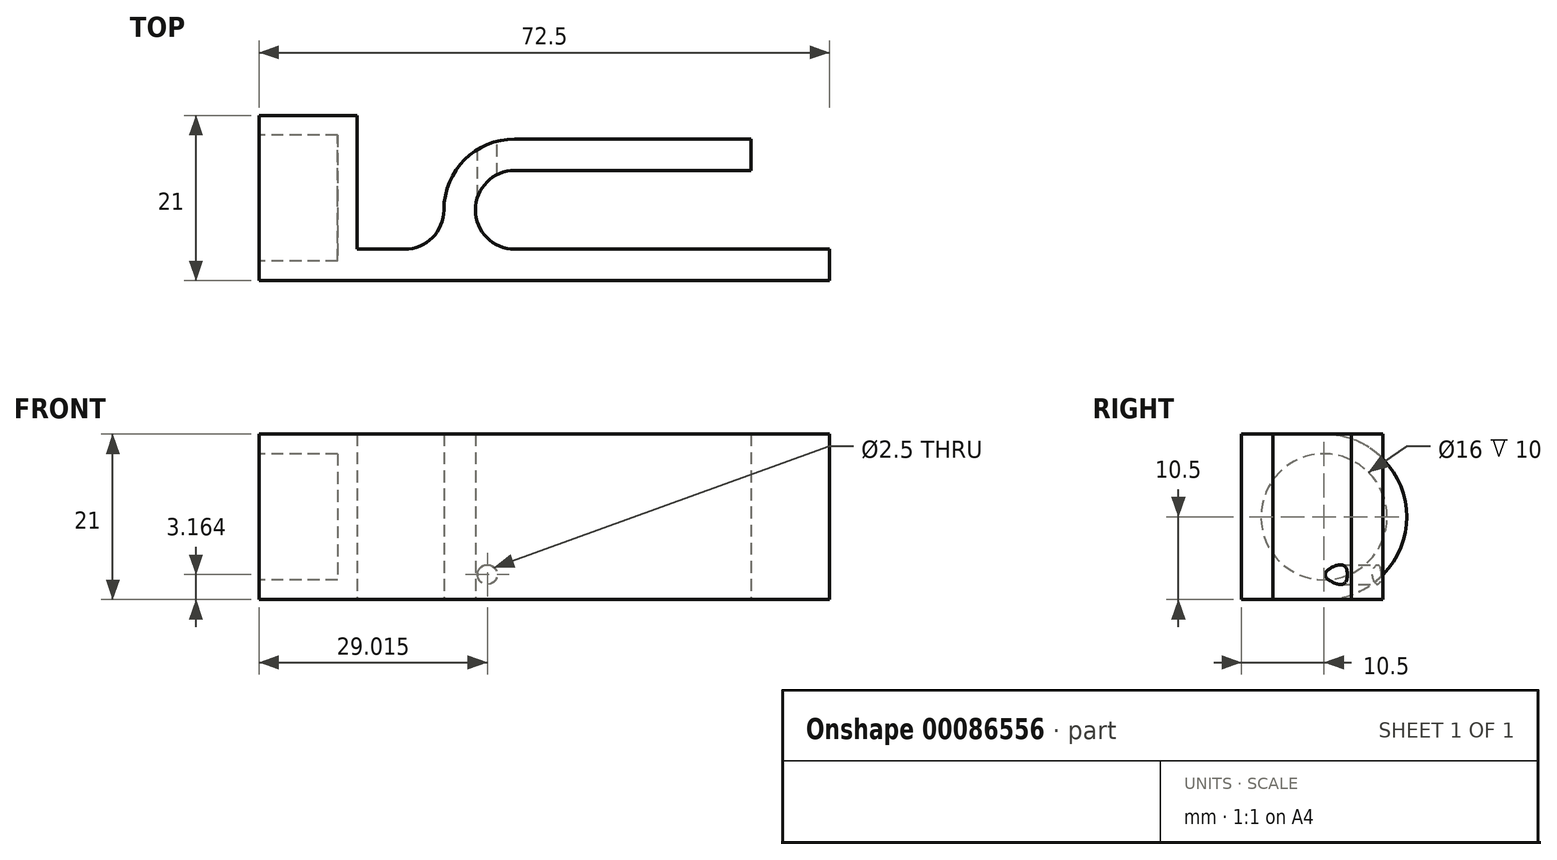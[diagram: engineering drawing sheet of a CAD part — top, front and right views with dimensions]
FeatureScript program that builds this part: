
annotation { "Feature Type Name" : "Feature", "Feature Type Description" : "" }
export const myFeature = defineFeature(function(context is Context, id is Id, definition is map)
    precondition{}
    {
        {
            var Q0;
            Q0=qCreatedBy(makeId("Top.planeOp"),FACE);
            var sketch = newSketch(context, id + "F0", { "sketchPlane" : qUnion([Q0])});
            skLineSegment(sketch, "E0", {"start": v(0, 0) * mm, "end": v(60, 0) * mm});
            skLineSegment(sketch, "E1", {"start": v(60, 0) * mm, "end": v(60, 4) * mm});
            skLineSegment(sketch, "E2", {"start": v(60, 4) * mm, "end": v(20, 4) * mm});
            skLineSegment(sketch, "E3", {"start": v(15, 9) * mm, "end": v(15, 9) * mm});
            skLineSegment(sketch, "E4", {"start": v(20, 14) * mm, "end": v(50, 14) * mm});
            skLineSegment(sketch, "E5", {"start": v(50, 14) * mm, "end": v(50, 18) * mm});
            skLineSegment(sketch, "E6", {"start": v(50, 18) * mm, "end": v(20, 18) * mm});
            skLineSegment(sketch, "E7", {"start": v(11, 9) * mm, "end": v(11, 9) * mm});
            skLineSegment(sketch, "E8", {"start": v(6, 4) * mm, "end": v(0, 4) * mm});
            skPoint(sketch, "E9.visualSharp", {"position": v(15, 14) * mm});
            skArc(sketch, "E9.filletArc", {"start": v(20, 14) * mm, "mid": v(16.46, 12.54) * mm, "end": v(15, 9) * mm});
            skPoint(sketch, "E10.visualSharp", {"position": v(11, 18) * mm});
            skArc(sketch, "E10.filletArc", {"start": v(20, 18) * mm, "mid": v(13.64, 15.36) * mm, "end": v(11, 9) * mm});
            skPoint(sketch, "E11.visualSharp", {"position": v(15, 4) * mm});
            skArc(sketch, "E11.filletArc", {"start": v(15, 9) * mm, "mid": v(16.46, 5.46) * mm, "end": v(20, 4) * mm});
            skPoint(sketch, "E12.visualSharp", {"position": v(11, 4) * mm});
            skArc(sketch, "E12.filletArc", {"start": v(6, 4) * mm, "mid": v(9.54, 5.46) * mm, "end": v(11, 9) * mm});
            skLineSegment(sketch, "E13", {"start": v(0, 4) * mm, "end": v(0, 0) * mm});
            skSolve(sketch);
        }
        {
            var Q0;
            Q0=makeQuery(id+"F0.imprint","IMPRINT",FACE,{"disambiguationData":[TD([[makeQuery(id+"F0.imprint","IMPRINT",EDGE,{"derivedFrom":sQuery(id+"F0.wireOp",EDGE,"E0")}),1.0]])]});
            extrude(context, id + "F1", {"entities" : qUnion([Q0]), "endBound" : BoundingType.SYMMETRIC, "depth" : 21 * mm});
        }
        {
            var Q0;
            Q0=qCreatedBy(makeId("Top.planeOp"),FACE);
            var sketch = newSketch(context, id + "F2", { "sketchPlane" : qUnion([Q0])});
            skLineSegment(sketch, "E14", {"start": v(0, 0) * mm, "end": v(-12.5, 0) * mm});
            skLineSegment(sketch, "E15", {"start": v(-12.5, 0) * mm, "end": v(-12.5, 2.5) * mm});
            skLineSegment(sketch, "E16", {"start": v(-12.5, 2.5) * mm, "end": v(-2.5, 2.5) * mm});
            skLineSegment(sketch, "E17", {"start": v(-2.5, 2.5) * mm, "end": v(-2.5, 10.5) * mm});
            skLineSegment(sketch, "E18", {"start": v(-2.5, 10.5) * mm, "end": v(0, 10.5) * mm});
            skLineSegment(sketch, "E19", {"start": v(0, 10.5) * mm, "end": v(0, 0) * mm});
            skSolve(sketch);
        }
        {
            var Q0;
            Q0=makeQuery(id+"F2.imprint","IMPRINT",FACE,{"disambiguationData":[TD([[makeQuery(id+"F2.imprint","IMPRINT",EDGE,{"derivedFrom":sQuery(id+"F2.wireOp",EDGE,"E14")}),-1.0]])]});
            var Q1;
            Q1=sQuery(id+"F2.wireOp",EDGE,"E18");
            revolve(context, id + "F3", {"operationType" : NewBodyOperationType.ADD, "entities" : qUnion([Q0]), "axis" : qUnion([Q1]), "revolveType" : RevolveType.FULL});
        }
        {
            var Q0;
            {var subQ0=sQuery(id+"F0.wireOp",EDGE,"E13");var subQ1=makeQuery(id+"F1.opExtrude","SWEPT_FACE",FACE,{"disambiguationData":[OSD([subQ0])]});var subQ2=sQuery(id+"F0.wireOp",EDGE,"E8");var subQ3=sQuery(id+"F0.wireOp",EDGE,"E0");Q0=makeQuery(id+"F3.boolean.opBoolean","SPLIT",FACE,{"disambiguationData":[TD([makeQuery(id+"F1.opExtrude","CAP_FACE",FACE,{"disambiguationData":[OSD([subQ3,sQuery(id+"F0.wireOp",EDGE,"E1"),sQuery(id+"F0.wireOp",EDGE,"E2"),sQuery(id+"F0.wireOp",EDGE,"E4"),sQuery(id+"F0.wireOp",EDGE,"E5"),sQuery(id+"F0.wireOp",EDGE,"E6"),subQ2,sQuery(id+"F0.wireOp",EDGE,"E9.filletArc"),sQuery(id+"F0.wireOp",EDGE,"E10.filletArc"),sQuery(id+"F0.wireOp",EDGE,"E11.filletArc"),sQuery(id+"F0.wireOp",EDGE,"E12.filletArc"),subQ0])],"isStart":false})])],"derivedFrom":subQ1});}
            var Q1;
            {var subQ0=sQuery(id+"F0.wireOp",EDGE,"E13");var subQ1=makeQuery(id+"F1.opExtrude","SWEPT_FACE",FACE,{"disambiguationData":[OSD([subQ0])]});var subQ2=sQuery(id+"F0.wireOp",EDGE,"E8");var subQ3=sQuery(id+"F0.wireOp",EDGE,"E0");Q1=makeQuery(id+"F3.boolean.opBoolean","SPLIT",FACE,{"disambiguationData":[TD([makeQuery(id+"F1.opExtrude","CAP_FACE",FACE,{"disambiguationData":[OSD([subQ3,sQuery(id+"F0.wireOp",EDGE,"E1"),sQuery(id+"F0.wireOp",EDGE,"E2"),sQuery(id+"F0.wireOp",EDGE,"E4"),sQuery(id+"F0.wireOp",EDGE,"E5"),sQuery(id+"F0.wireOp",EDGE,"E6"),subQ2,sQuery(id+"F0.wireOp",EDGE,"E9.filletArc"),sQuery(id+"F0.wireOp",EDGE,"E10.filletArc"),sQuery(id+"F0.wireOp",EDGE,"E11.filletArc"),sQuery(id+"F0.wireOp",EDGE,"E12.filletArc"),subQ0])],"isStart":true})])],"derivedFrom":subQ1});}
            extrude(context, id + "F4", {"entities" : qUnion([Q0, Q1]), "operationType" : NewBodyOperationType.ADD, "depth" : 12.5 * mm});
        }
        {
            var Q0;
            {var subQ0=sQuery(id+"F0.wireOp",EDGE,"E13");var subQ1=makeQuery(id+"F1.opExtrude","SWEPT_FACE",FACE,{"disambiguationData":[OSD([subQ0])]});var subQ3=sQuery(id+"F0.wireOp",EDGE,"E8");var subQ5=sQuery(id+"F0.wireOp",EDGE,"E12.filletArc");var subQ6=sQuery(id+"F0.wireOp",EDGE,"E11.filletArc");var subQ7=sQuery(id+"F0.wireOp",EDGE,"E10.filletArc");var subQ8=sQuery(id+"F0.wireOp",EDGE,"E9.filletArc");var subQ9=sQuery(id+"F0.wireOp",EDGE,"E6");var subQ10=sQuery(id+"F0.wireOp",EDGE,"E5");var subQ11=sQuery(id+"F0.wireOp",EDGE,"E4");var subQ12=sQuery(id+"F0.wireOp",EDGE,"E2");var subQ13=sQuery(id+"F0.wireOp",EDGE,"E1");var subQ14=sQuery(id+"F0.wireOp",EDGE,"E0");Q0=makeQuery(id+"F4.boolean.opBoolean","MERGE",FACE,{"derivedFrom":[makeQuery(id+"F3.opRevolve","SWEPT_FACE",FACE,{"disambiguationData":[OSD([sQuery(id+"F2.wireOp",EDGE,"E15")])]}),makeQuery(id+"F4.opExtrude","CAP_FACE",FACE,{"disambiguationData":[OSD([subQ0]),TDD([makeQuery(id+"F3.boolean.opBoolean","SPLIT",FACE,{"disambiguationData":[TD([makeQuery(id+"F1.opExtrude","CAP_FACE",FACE,{"disambiguationData":[OSD([subQ14,subQ13,subQ12,subQ11,subQ10,subQ9,subQ3,subQ8,subQ7,subQ6,subQ5,subQ0])],"isStart":true})])],"derivedFrom":subQ1})])],"isStart":false}),makeQuery(id+"F4.opExtrude","CAP_FACE",FACE,{"disambiguationData":[OSD([subQ0]),TDD([makeQuery(id+"F3.boolean.opBoolean","SPLIT",FACE,{"disambiguationData":[TD([makeQuery(id+"F1.opExtrude","CAP_FACE",FACE,{"disambiguationData":[OSD([subQ14,subQ13,subQ12,subQ11,subQ10,subQ9,subQ3,subQ8,subQ7,subQ6,subQ5,subQ0])],"isStart":false})])],"derivedFrom":subQ1})])],"isStart":false})]});}
            var sketch = newSketch(context, id + "F5", { "sketchPlane" : qUnion([Q0])});
            skLineSegment(sketch, "E20", {"start": v(-4, -8.25) * mm, "end": v(-4, -10.5) * mm});
            skLineSegment(sketch, "E21", {"start": v(-4, -10.5) * mm, "end": v(-10.5, -10.5) * mm});
            skArc(sketch, "E22", {"start": v(-10.5, -10.5) * mm, "mid": v(-7.06, -9.92) * mm, "end": v(-4, -8.25) * mm});
            skArc(sketch, "E23.MirrorCS", {"start": v(-10.5, 10.5) * mm, "mid": v(-7.06, 9.92) * mm, "end": v(-4, 8.25) * mm});
            skLineSegment(sketch, "E24.MirrorCS", {"start": v(-4, 10.5) * mm, "end": v(-10.5, 10.5) * mm});
            skLineSegment(sketch, "E25.MirrorCS", {"start": v(-4, 8.25) * mm, "end": v(-4, 10.5) * mm});
            skSolve(sketch);
        }
        {
            var Q0;
            Q0 = qSketchRegion(id + "F5", true);
            extrude(context, id + "F6", {"entities" : qUnion([Q0]), "operationType" : NewBodyOperationType.ADD, "oppositeDirection" : true, "depth" : 12.5 * mm});
        }
        {
            var Q0;
            Q0=makeQuery(id+"F1.opExtrude","SWEPT_FACE",FACE,{"disambiguationData":[OSD([sQuery(id+"F0.wireOp",EDGE,"E6")])]});
            var sketch = newSketch(context, id + "F7", { "sketchPlane" : qUnion([Q0])});
            skCircle(sketch, "E26", {"center": v(20.34, 29.12) * mm, "radius": 1.6 * mm});
            skCircle(sketch, "E27", {"center": v(-16.52, -7.34) * mm, "radius": 1.25 * mm});
            skSolve(sketch);
        }
        {
            var Q0;
            Q0=sQuery(id+"F7.wireOp",VERTEX,"rPzcs4XO-guIr-8GQG-JvGF-6TBGIbvZQWbU.center");
            var Q1;
            Q1=sQuery(id+"F7.wireOp",VERTEX,"E27.center");
            var Q2;
            Q2=makeQuery(id+"F1.opExtrude","SWEPT_BODY",BODY,{"disambiguationData":[OSD([sQuery(id+"F0.wireOp",EDGE,"E0"),sQuery(id+"F0.wireOp",EDGE,"E1"),sQuery(id+"F0.wireOp",EDGE,"E2"),sQuery(id+"F0.wireOp",EDGE,"E4"),sQuery(id+"F0.wireOp",EDGE,"E5"),sQuery(id+"F0.wireOp",EDGE,"E6"),sQuery(id+"F0.wireOp",EDGE,"E8"),sQuery(id+"F0.wireOp",EDGE,"E9.filletArc"),sQuery(id+"F0.wireOp",EDGE,"E10.filletArc"),sQuery(id+"F0.wireOp",EDGE,"E11.filletArc"),sQuery(id+"F0.wireOp",EDGE,"E12.filletArc"),sQuery(id+"F0.wireOp",EDGE,"E13")])]});
            hole(context, id + "F8", {"style" : HoleStyle.SIMPLE, "endStyle" : HoleEndStyle.BLIND, "holeDiameter" : 2.5 * mm, "holeDepth" : 6 * mm, "locations" : qUnion([Q0, Q1]), "scope" : qUnion([Q2])});
        }
    });
